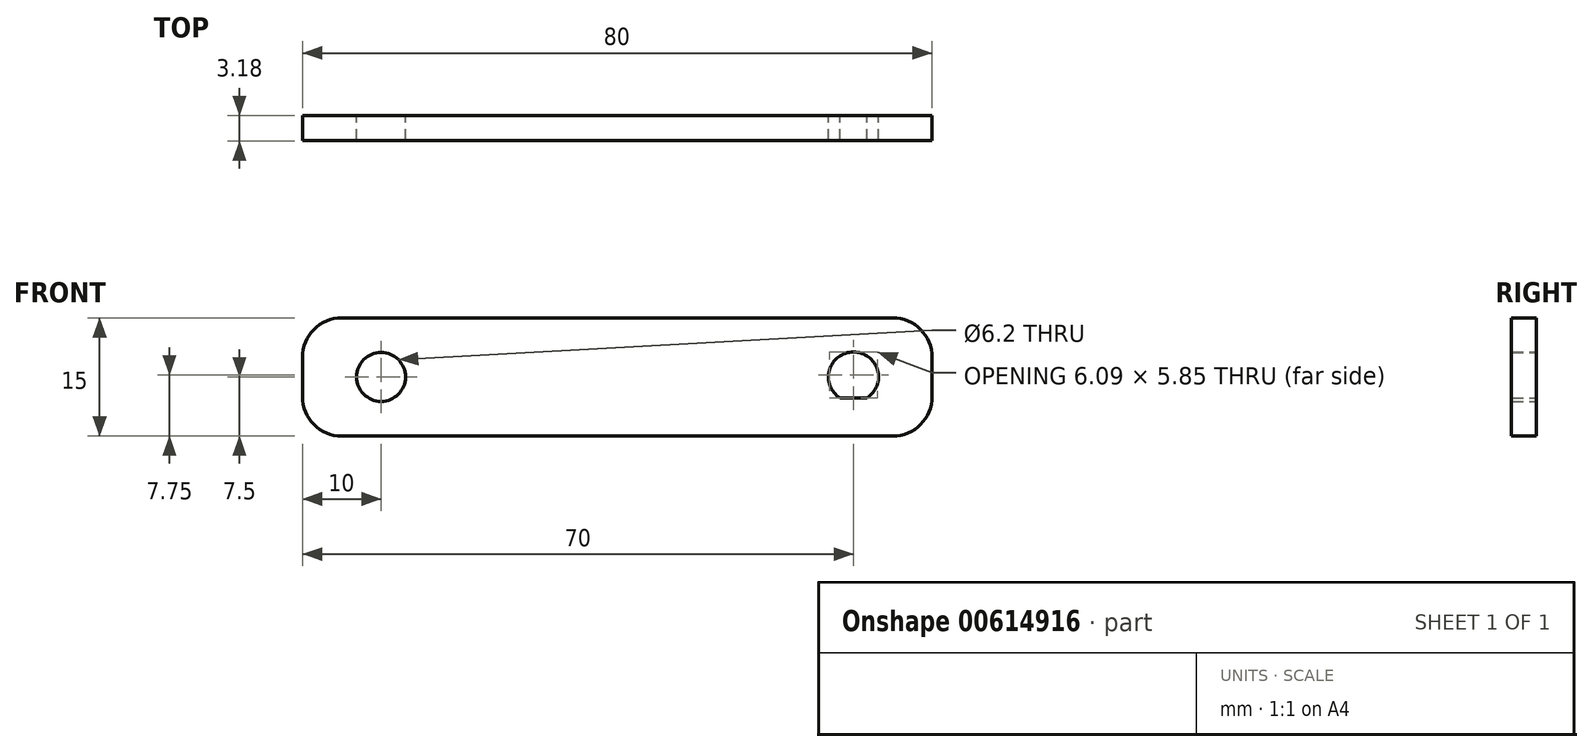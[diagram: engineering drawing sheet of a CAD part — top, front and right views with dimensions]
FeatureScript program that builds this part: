
annotation { "Feature Type Name" : "Feature", "Feature Type Description" : "" }
export const myFeature = defineFeature(function(context is Context, id is Id, definition is map)
    precondition{}
    {
        {
            var Q0;
            Q0=qCreatedBy(makeId("Front.planeOp"),FACE);
            var sketch = newSketch(context, id + "F0", { "sketchPlane" : qUnion([Q0])});
            skLineSegment(sketch, "E0.bottom", {"start": v(35, 7.5) * mm, "end": v(-35, 7.5) * mm});
            skLineSegment(sketch, "E0.top", {"start": v(35, -7.5) * mm, "end": v(-35, -7.5) * mm});
            skLineSegment(sketch, "E0.left", {"start": v(40, 2.5) * mm, "end": v(40, -2.5) * mm});
            skLineSegment(sketch, "E0.right", {"start": v(-40, 2.5) * mm, "end": v(-40, -2.5) * mm});
            skPoint(sketch, "E0.middle", {"position": v(0, 0) * mm});
            skLineSegment(sketch, "E1", {"start": v(0, 0) * mm, "end": v(-30, 0) * mm});
            skCircle(sketch, "E2", {"center": v(-30, 0) * mm, "radius": 3.1 * mm});
            skPoint(sketch, "E3.visualSharp", {"position": v(-40, 7.5) * mm});
            skArc(sketch, "E3.filletArc", {"start": v(-35, 7.5) * mm, "mid": v(-38.54, 6.04) * mm, "end": v(-40, 2.5) * mm});
            skPoint(sketch, "E4.visualSharp", {"position": v(-40, -7.5) * mm});
            skArc(sketch, "E4.filletArc", {"start": v(-40, -2.5) * mm, "mid": v(-38.54, -6.04) * mm, "end": v(-35, -7.5) * mm});
            skPoint(sketch, "E5.visualSharp", {"position": v(40, 7.5) * mm});
            skArc(sketch, "E5.filletArc", {"start": v(40, 2.5) * mm, "mid": v(38.54, 6.04) * mm, "end": v(35, 7.5) * mm});
            skPoint(sketch, "E6.visualSharp", {"position": v(40, -7.5) * mm});
            skArc(sketch, "E6.filletArc", {"start": v(35, -7.5) * mm, "mid": v(38.54, -6.04) * mm, "end": v(40, -2.5) * mm});
            skLineSegment(sketch, "E7", {"start": v(30, 0) * mm, "end": v(0, 0) * mm});
            skLineSegment(sketch, "E8", {"start": v(28.29, -2.67) * mm, "end": v(31.71, -2.67) * mm});
            skArc(sketch, "E9", {"start": v(31.71, -2.67) * mm, "mid": v(30, 3.17) * mm, "end": v(28.29, -2.67) * mm});
            skSolve(sketch);
        }
        {
            var Q0;
            Q0=makeQuery(id+"F0.imprint","IMPRINT",FACE,{"disambiguationData":[TD([[makeQuery(id+"F0.imprint","IMPRINT",EDGE,{"derivedFrom":sQuery(id+"F0.wireOp",EDGE,"E0.bottom")}),1.0]])]});
            extrude(context, id + "F1", {"entities" : qUnion([Q0]), "depth" : 3.17 * mm, "offsetDistance" : 25 * mm});
        }
    });
